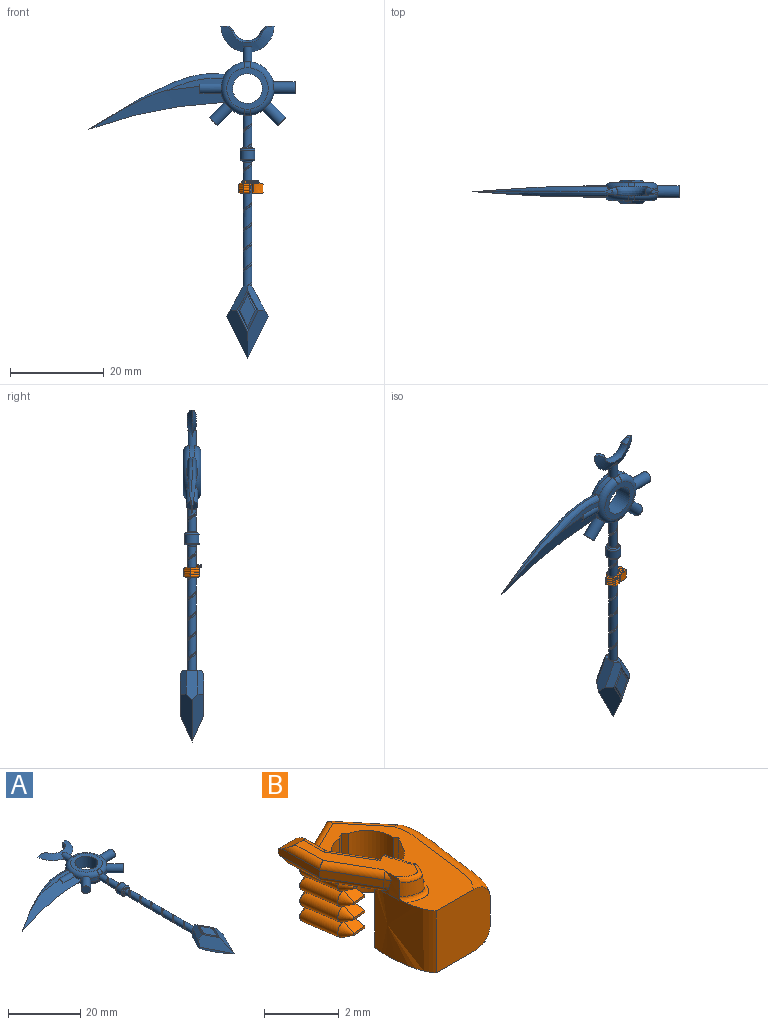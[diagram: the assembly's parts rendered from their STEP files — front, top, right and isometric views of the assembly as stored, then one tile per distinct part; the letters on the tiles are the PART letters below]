
ASSEMBLY  parts=2 mates=1
PART A: 95 faces, bbox 47.1x71.3x5.4 mm
  f0: cylinder r=0.95mm len=6.92mm, axis (0,1,0), area 36.3mm2, adj f1,f2,f3,f6,f20,f23,f67,f69
  f1: bspline ~8.16x2.41mm, area 3.9mm2, adj f0,f2,f3,f37,f38,f67,f68,f69
  f2: bspline ~8.15x2.45mm, area 3.9mm2, adj f0,f1,f20,f37,f38,f67
  f3: cylinder r=5.71mm len=2.59mm, axis (0,0,-1), area 3.2mm2, adj f0,f1,f12,f13,f35,f37
  f4: cylinder r=5.71mm len=2.11mm, axis (0,0,-1), area 0.8mm2, adj f13,f35,f40,f44
  f5: cylinder r=3.17mm len=6.35mm, axis (0,0,-1), area 76mm2, adj f16,f17
  f6: cylinder r=5.71mm len=2.59mm, axis (0,0,-1), area 3.2mm2, adj f0,f8,f9,f33
  f7: cylinder r=5.71mm len=2.11mm, axis (0,0,-1), area 2.6mm2, adj f8,f9,f25,f33
  f8: torus R=4.45mm, axis (0,0,1), area 28.3mm2, adj f6,f7,f15,f17,f20,f21,f25,f33
  f9: torus R=4.45mm, axis (0,0,1), area 28.3mm2, adj f6,f7,f15,f16,f22,f23,f25,f33
  f10: cylinder r=5.71mm len=4.27mm, axis (0,0,-1), area 6.4mm2, adj f12,f13,f19,f41,f42
  f11: cylinder r=5.71mm len=2.11mm, axis (0,0,-1), area 0.8mm2, adj f12,f35,f39,f45
  f12: torus R=4.45mm, axis (0,0,1), area 27.6mm2, adj f3,f10,f11,f17,f20,f21,f32,f35
  f13: torus R=4.45mm, axis (0,0,1), area 27.7mm2, adj f3,f4,f10,f16,f22,f23,f31,f35
  f14: plane 1.74x0.58mm, normal (0,1,0), area 0.4mm2, adj f19,f26
  f15: cylinder r=5.71mm len=4.87mm, axis (0,0,-1), area 8.6mm2, adj f8,f9,f19,f25
  f16: plane 8.97x8.89mm, normal (0,0,1), area 30.4mm2, adj f5,f9,f13,f22,f23
  f17: plane 8.97x8.89mm, normal (0,0,-1), area 30.4mm2, adj f5,f8,f12,f20,f21
  f18: plane 1.66x0.52mm, normal (0,1,0), area 0.4mm2, adj f19,f27
  f19: cylinder r=0.95mm len=3.3mm, axis (0,1,0), area 18.3mm2, adj f10,f14,f15,f18,f21,f22,f26,f27
  f20: bspline ~1.53x1.35mm, area 2.3mm2, adj f0,f2,f8,f12,f17,f37
  f21: bspline ~1.42x1.3mm, area 2.3mm2, adj f8,f12,f17,f19
  f22: bspline ~1.42x1.3mm, area 2.3mm2, adj f9,f13,f16,f19
  f23: bspline ~1.42x1.3mm, area 2.3mm2, adj f0,f9,f13,f16
  f24: plane 2.54x2.54mm, normal (1,0,0), area 5.1mm2, adj f25
  f25: cylinder r=1.27mm len=4.58mm, axis (-1,0,0), area 36.3mm2, adj f7,f8,f9,f15,f24
  f26: bspline ~11.33x5.46mm, area 29.7mm2, adj f14,f19,f27,f28,f29,f30,f93,f94
  f27: bspline ~11.33x5.46mm, area 30.2mm2, adj f18,f19,f26,f28,f29,f30,f93,f94
  f28: plane 1.88x1.27mm, normal (0.01,1,0), area 0.8mm2, adj f26,f27,f94
  f29: plane 1.84x1.25mm, normal (0.01,1,0), area 0.7mm2, adj f26,f27,f93
  f30: bspline ~7.14x7.14mm, area 18.5mm2, adj f26,f27,f93,f94
  f31: plane 12.18x2.8mm, normal (0,0,1), area 11.7mm2, adj f13,f40,f41,f43,f44
  f32: plane 12.19x2.81mm, normal (0,0,-1), area 11.7mm2, adj f12,f39,f42,f45,f46
  f33: cylinder r=1.27mm len=5.04mm, axis (-0.71,0.71,0), area 36.3mm2, adj f6,f7,f8,f9,f34
  f34: plane 2.54x1.8mm, normal (0.71,-0.71,0), area 5.1mm2, adj f33
  f35: cylinder r=1.27mm len=5.06mm, axis (0.71,0.71,0), area 36.2mm2, adj f3,f4,f11,f12,f13,f36
  f36: plane 2.54x1.8mm, normal (-0.71,-0.71,0), area 5.1mm2, adj f35
  f37: bspline ~2.13x1.59mm, area 0.5mm2, adj f1,f2,f3,f12,f20,f38
  f38: plane 0.71x0.37mm, normal (0,0,-1), area 0.1mm2, adj f1,f2,f37
  f39: bspline ~33.29x10.15mm, area 73.1mm2, adj f11,f32,f40,f42,f45,f46
  f40: bspline ~33.29x10.15mm, area 73mm2, adj f4,f31,f39,f41,f43,f44
  f41: bspline ~30.28x13.43mm, area 35.4mm2, adj f10,f13,f31,f40,f42
  f42: bspline ~30.28x13.43mm, area 35.4mm2, adj f10,f12,f32,f39,f41
  f43: plane 1.87x0.64mm, normal (-1,0,0), area 0.5mm2, adj f31,f40,f44
  f44: cylinder r=1.27mm len=4.58mm, axis (1,0,0), area 10.1mm2, adj f4,f13,f31,f40,f43
  f45: cylinder r=1.27mm len=4.58mm, axis (1,0,0), area 10.1mm2, adj f11,f12,f32,f39,f46
  f46: plane 1.87x0.64mm, normal (-1,0,0), area 0.5mm2, adj f32,f39,f45
  f47: plane 2.57x2.57mm, normal (0,1,0), area 0.2mm2, adj f67,f68,f69,f74
  f48: plane 2.57x2.57mm, normal (0,-1,0), area 0.2mm2, adj f70,f71,f72,f73
  f49: cylinder r=1.59mm len=3.18mm, axis (0,-1,0), area 19.3mm2, adj f73,f74
  f50: plane 10.2x4.46mm, normal (-0.63,-0.32,0.71), area 28.3mm2, adj f51,f53,f57,f58,f78
  f51: plane 10.2x4.46mm, normal (-0.63,-0.32,-0.71), area 28.3mm2, adj f50,f52,f55,f58,f84
  f52: plane 5.16x3.72mm, normal (-0.62,0.34,-0.71), area 10.1mm2, adj f51,f54,f58,f59,f85
  f53: plane 10.2x4.46mm, normal (0.63,-0.32,0.71), area 28.3mm2, adj f50,f55,f56,f61,f79
  f54: plane 5.16x3.72mm, normal (0.62,0.34,-0.71), area 10.1mm2, adj f52,f55,f60,f61,f86
  f55: plane 10.2x4.46mm, normal (0.63,-0.32,-0.71), area 28.3mm2, adj f51,f53,f54,f61,f91
  f56: plane 5.16x3.72mm, normal (0.62,0.34,0.71), area 10.1mm2, adj f53,f57,f61,f62,f80
  f57: plane 5.16x3.72mm, normal (-0.62,0.34,0.71), area 10.1mm2, adj f50,f56,f58,f63,f81
  f58: plane 6.48x3.56mm, normal (-0.88,0.48,0), area 16.7mm2, adj f50,f51,f52,f57,f59,f63,f66
  f59: plane 1.93x0.96mm, normal (-0.06,1,0), area 0.9mm2, adj f52,f58,f60,f66
  f60: plane 1.93x0.96mm, normal (0.06,1,0), area 0.9mm2, adj f54,f59,f61,f66
  f61: plane 6.48x3.56mm, normal (0.88,0.48,0), area 16.7mm2, adj f53,f54,f55,f56,f60,f62,f66
  f62: plane 1.94x0.96mm, normal (0.06,1,0), area 0.9mm2, adj f56,f61,f63,f64,f65,f66
  f63: plane 1.93x0.95mm, normal (-0.06,1,0), area 0.9mm2, adj f57,f58,f62,f64,f66
  f64: bspline ~28x2.45mm, area 13.4mm2, adj f62,f63,f65,f66,f70,f71,f72
  f65: bspline ~28.02x2.41mm, area 13.8mm2, adj f62,f64,f66,f71
  f66: cylinder r=0.95mm len=26.59mm, axis (0,1,0), area 134.4mm2, adj f58,f59,f60,f61,f62,f63,f64,f65
  f67: bspline ~0.85x0.81mm, area 0.2mm2, adj f0,f1,f2,f47,f68,f69
  f68: bspline ~0.61x0.46mm, area 0.1mm2, adj f1,f47,f67,f69
  f69: torus R=1.26mm, axis (0,-1,0), area 3mm2, adj f0,f1,f47,f67,f68
  f70: bspline ~0.57x0.49mm, area 0.1mm2, adj f48,f64,f71,f72
  f71: bspline ~0.85x0.75mm, area 0.2mm2, adj f48,f64,f65,f66,f70,f72
  f72: torus R=1.26mm, axis (0,-1,0), area 3mm2, adj f48,f64,f66,f70,f71
  f73: torus R=1.28mm, axis (0,-1,0), area 4.4mm2, adj f48,f49
  f74: torus R=1.28mm, axis (0,-1,0), area 4.4mm2, adj f47,f49
  f75: plane 3.66x2mm, normal (-0.62,0.34,0.71), area 1.4mm2, adj f76,f81,f82,f83
  f76: plane 3.66x2mm, normal (0.62,0.34,0.71), area 1.4mm2, adj f75,f77,f80,f83
  f77: plane 3.96x2mm, normal (0.63,-0.32,0.71), area 1.5mm2, adj f76,f79,f82,f83
  f78: plane 4.53x2.28mm, normal (0.63,0.32,0.71), area 1.7mm2, adj f50,f79,f81,f82
  f79: plane 4.53x2.28mm, normal (-0.63,0.32,0.71), area 1.7mm2, adj f53,f77,f78,f80
  f80: plane 4.18x2.28mm, normal (-0.62,-0.34,0.71), area 1.6mm2, adj f56,f76,f79,f81
  f81: plane 4.18x2.28mm, normal (0.62,-0.34,0.71), area 1.6mm2, adj f57,f75,f78,f80
  f82: plane 3.96x2mm, normal (-0.63,-0.32,0.71), area 1.5mm2, adj f75,f77,f78,f83
  f83: plane 6.52x3.42mm, normal (0,0,1), area 11.1mm2, adj f75,f76,f77,f82
  f84: plane 4.53x2.28mm, normal (0.63,0.32,-0.71), area 1.7mm2, adj f51,f85,f90,f91
  f85: plane 4.18x2.28mm, normal (0.62,-0.34,-0.71), area 1.6mm2, adj f52,f84,f86,f89
  f86: plane 4.18x2.28mm, normal (-0.62,-0.34,-0.71), area 1.6mm2, adj f54,f85,f88,f91
  f87: plane 3.96x2mm, normal (0.63,-0.32,-0.71), area 1.5mm2, adj f88,f90,f91,f92
  f88: plane 3.66x2mm, normal (0.62,0.34,-0.71), area 1.4mm2, adj f86,f87,f89,f92
  f89: plane 3.66x2mm, normal (-0.62,0.34,-0.71), area 1.4mm2, adj f85,f88,f90,f92
  f90: plane 3.96x2mm, normal (-0.63,-0.32,-0.71), area 1.5mm2, adj f84,f87,f89,f92
  f91: plane 4.53x2.28mm, normal (-0.63,0.32,-0.71), area 1.7mm2, adj f55,f84,f86,f87
  f92: plane 6.52x3.42mm, normal (0,0,-1), area 11.1mm2, adj f87,f88,f89,f90
  f93: bspline ~2.68x1.63mm, area 2.6mm2, adj f26,f27,f29,f30
  f94: bspline ~2.79x1.69mm, area 2.8mm2, adj f26,f27,f28,f30
PART B: 79 faces, bbox 4.3x5.7x2.9 mm
  f0: plane 4.84x2.76mm, normal (0,0,-1), area 6.7mm2, adj f5,f6,f7,f8,f9,f10,f12,f16
  f1: plane 0.22x0.13mm, normal (0.98,0.2,0), area 0mm2, adj f10,f19,f23,f76
  f2: plane 0.22x0.13mm, normal (0.98,0.2,0), area 0mm2, adj f25,f29,f30,f76
  f3: plane 0.22x0.13mm, normal (0.98,0.2,0), area 0mm2, adj f32,f36,f37,f76
  f4: plane 0.22x0.13mm, normal (0.98,0.2,0), area 0mm2, adj f39,f43,f44,f76
  f5: plane 2.03x0.23mm, normal (0.98,0.2,0), area 0.5mm2, adj f0,f7,f11,f76
  f6: plane 2.03x0.21mm, normal (0.51,-0.86,0), area 0.5mm2, adj f0,f9,f11,f78
  f7: plane 2.03x0.2mm, normal (0.51,-0.86,0), area 0.5mm2, adj f0,f5,f11,f78
  f8: plane 2.03x0.12mm, normal (-0.8,-0.6,0), area 0.3mm2, adj f0,f11,f12,f77
  f9: plane 2.03x0.14mm, normal (-0.8,-0.6,0), area 0.4mm2, adj f0,f6,f11,f77
  f10: plane 0.47x0.41mm, normal (0.04,-0.5,-0.87), area 0.2mm2, adj f0,f1,f19,f24,f76
  f11: plane 4.94x2.78mm, normal (0,0,1), area 5.2mm2, adj f5,f6,f7,f8,f9,f12,f16,f17
  f12: extruded ~2.03x2.02mm, area 5mm2, adj f0,f8,f11,f17,f48,f69
  f13: extruded ~0.41x0.37mm, area 0.1mm2, adj f18,f35,f42,f46
  f14: extruded ~0.51x0.37mm, area 0.1mm2, adj f18,f28,f35
  f15: extruded ~0.41x0.37mm, area 0.1mm2, adj f18,f22,f28,f47
  f16: plane 2.18x2.18mm, normal (0,-1,0), area 4mm2, adj f0,f11,f17,f18,f46,f47
  f17: extruded ~2.05x2.01mm, area 4.2mm2, adj f0,f11,f12,f16,f48,f70,f72
  f18: extruded ~3.28x1.02mm, area 3.4mm2, adj f13,f14,f15,f16,f46,f47
  f19: plane 0.48x0.07mm, normal (0.07,-1,0), area 0mm2, adj f1,f10,f23,f24
  f20: cylinder r=0.25mm len=1.12mm, axis (-0.14,0.99,0), area 0.9mm2, adj f0,f21,f24,f26
  f21: cylinder r=0.25mm len=1.76mm, axis (0.9,0.44,0), area 1.5mm2, adj f0,f20,f22,f27
  f22: cylinder r=0.25mm len=2.02mm, axis (0.64,-0.77,0), area 1.7mm2, adj f0,f15,f21,f28,f47
  f23: plane 0.47x0.41mm, normal (0.04,-0.5,0.87), area 0.2mm2, adj f1,f19,f24,f29,f76
  f24: bspline ~0.52x0.38mm, area 0.2mm2, adj f10,f19,f20,f23
  f25: plane 0.48x0.07mm, normal (0.07,-1,0), area 0mm2, adj f2,f29,f30,f31
  f26: cylinder r=0.25mm len=1.12mm, axis (-0.14,0.99,0), area 0.9mm2, adj f20,f27,f31,f33
  f27: cylinder r=0.25mm len=1.76mm, axis (0.9,0.44,0), area 1.5mm2, adj f21,f26,f28,f34
  f28: cylinder r=0.25mm len=1.88mm, axis (0.64,-0.77,0), area 1.7mm2, adj f14,f15,f22,f27,f35
  f29: plane 0.47x0.41mm, normal (0.04,-0.5,-0.87), area 0.2mm2, adj f2,f23,f25,f31,f76
  f30: plane 0.47x0.41mm, normal (0.04,-0.5,0.87), area 0.2mm2, adj f2,f25,f31,f36,f76
  f31: bspline ~0.52x0.38mm, area 0.2mm2, adj f25,f26,f29,f30
  f32: plane 0.48x0.07mm, normal (0.07,-1,0), area 0mm2, adj f3,f36,f37,f38
  f33: cylinder r=0.25mm len=1.12mm, axis (-0.14,0.99,0), area 0.9mm2, adj f26,f34,f38,f40
  f34: cylinder r=0.25mm len=1.76mm, axis (0.9,0.44,0), area 1.5mm2, adj f27,f33,f35,f41
  f35: cylinder r=0.25mm len=1.88mm, axis (0.64,-0.77,0), area 1.7mm2, adj f13,f14,f28,f34,f42
  f36: plane 0.47x0.41mm, normal (0.04,-0.5,-0.87), area 0.2mm2, adj f3,f30,f32,f38,f76
  f37: plane 0.47x0.41mm, normal (0.04,-0.5,0.87), area 0.2mm2, adj f3,f32,f38,f43,f76
  f38: bspline ~0.52x0.38mm, area 0.2mm2, adj f32,f33,f36,f37
  f39: plane 0.48x0.07mm, normal (0.07,-1,0), area 0mm2, adj f4,f43,f44,f45
  f40: cylinder r=0.25mm len=1.3mm, axis (0.14,-0.99,0), area 1mm2, adj f11,f33,f41,f45,f48
  f41: cylinder r=0.25mm len=2.11mm, axis (-0.9,-0.44,0), area 1.7mm2, adj f11,f34,f40,f42,f48
  f42: cylinder r=0.25mm len=2.02mm, axis (-0.64,0.77,0), area 1.7mm2, adj f11,f13,f35,f41,f46
  f43: plane 0.47x0.41mm, normal (0.04,-0.5,-0.87), area 0.2mm2, adj f4,f37,f39,f45,f76
  f44: plane 0.48x0.41mm, normal (0.04,-0.5,0.87), area 0.2mm2, adj f4,f11,f39,f45,f48,f76
  f45: bspline ~0.52x0.38mm, area 0.2mm2, adj f39,f40,f43,f44
  f46: bspline ~4.29x1.18mm, area 2.8mm2, adj f11,f13,f16,f18,f42
  f47: bspline ~4.29x1.18mm, area 2.8mm2, adj f0,f15,f16,f18,f22
  f48: plane 2.43x1.13mm, normal (0,0,-1), area 1mm2, adj f12,f17,f40,f41,f44,f54,f56,f61
  f49: extruded ~0.25x0.05mm, area 0mm2, adj f51,f54,f57,f69
  f50: plane 0.25x0.17mm, normal (-0.87,-0.5,0), area 0mm2, adj f52,f55,f58,f70
  f51: bspline ~1.06x0.66mm, area 0mm2, adj f49,f62,f66,f69
  f52: cylinder r=0.19mm len=0.24mm, axis (0.5,-0.87,0), area 0mm2, adj f50,f53,f70
  f53: cylinder r=0.19mm len=1.64mm, axis (0.5,-0.87,0), area 0.5mm2, adj f52,f58,f62,f67,f70
  f54: bspline ~3.19x1.76mm, area 0.3mm2, adj f11,f48,f49,f57,f61,f69
  f55: cylinder r=0.19mm len=0.14mm, axis (-0.5,0.87,0), area 0mm2, adj f50,f56,f70
  f56: cylinder r=0.19mm len=1.64mm, axis (-0.5,0.87,0), area 0.5mm2, adj f48,f55,f58,f68,f70
  f57: plane 1.26x0.73mm, normal (0.87,0.5,0), area 0.5mm2, adj f49,f54,f61,f66
  f58: plane 1.54x0.89mm, normal (-0.87,-0.5,0), area 0.5mm2, adj f50,f53,f56,f59
  f59: plane 1.54x0.25mm, normal (-1,-0.03,0), area 0.4mm2, adj f58,f60,f63,f64,f67,f68
  f60: plane 0.7x0.13mm, normal (0,1,0), area 0.1mm2, adj f59,f61,f63,f64
  f61: plane 1.42x0.45mm, normal (1,0,0), area 0.5mm2, adj f11,f48,f54,f57,f60,f63,f64,f65
  f62: plane 3.34x1.7mm, normal (0,0,1), area 1.5mm2, adj f51,f53,f64,f65,f66,f67,f69,f70
  f63: plane 0.84x0.58mm, normal (0,0.5,-0.87), area 0.3mm2, adj f48,f59,f60,f61,f68
  f64: plane 0.84x0.58mm, normal (0,0.5,0.87), area 0.3mm2, adj f59,f60,f61,f62,f65,f67
  f65: cylinder r=0.19mm len=1.1mm, axis (0,1,0), area 0.3mm2, adj f61,f62,f64,f66
  f66: cylinder r=0.19mm len=1.4mm, axis (-0.5,0.87,0), area 0.4mm2, adj f51,f57,f62,f65
  f67: cylinder r=0.19mm len=1.44mm, axis (0.03,-1,0), area 0.4mm2, adj f53,f59,f62,f64
  f68: cylinder r=0.19mm len=1.44mm, axis (-0.03,1,0), area 0.4mm2, adj f48,f56,f59,f63
  f69: bspline ~0.7x0.69mm, area 0.2mm2, adj f12,f49,f51,f54,f62,f71,f72,f75
  f70: bspline ~0.95x0.69mm, area 0.3mm2, adj f17,f50,f52,f53,f55,f56,f62,f71
  f71: bspline ~1.52x1.01mm, area 0.9mm2, adj f69,f70,f72,f73,f74,f75
  f72: bspline ~1.93x1.43mm, area 0.4mm2, adj f11,f17,f69,f70,f71
  f73: bspline ~1.05x0.52mm, area 0.2mm2, adj f62,f70,f71,f74
  f74: bspline ~0.13x0.11mm, area 0mm2, adj f71,f73,f75
  f75: bspline ~1.01x0.41mm, area 0.2mm2, adj f62,f69,f71,f74
  f76: cylinder r=0.95mm len=2.03mm, axis (0,0,-1), area 1.4mm2, adj f0,f1,f2,f3,f4,f5,f10,f11
  f77: cylinder r=0.95mm len=2.03mm, axis (0,0,-1), area 2.7mm2, adj f0,f8,f9,f11
  f78: cylinder r=0.95mm len=2.03mm, axis (0,0,-1), area 1.7mm2, adj f0,f6,f7,f11
PLACE A rot(axis=(1,0,0),90deg) t=(-9.89,-21.28,26.33)mm fixed
PLACE B rot(axis=(0,0,1),90deg) t=(-9.89,-21.28,-4.97)mm
MATE slider B.f76 <-> A.f0  axis (0,0,-1) through (-9.89,-21.28,-2.94)mm
